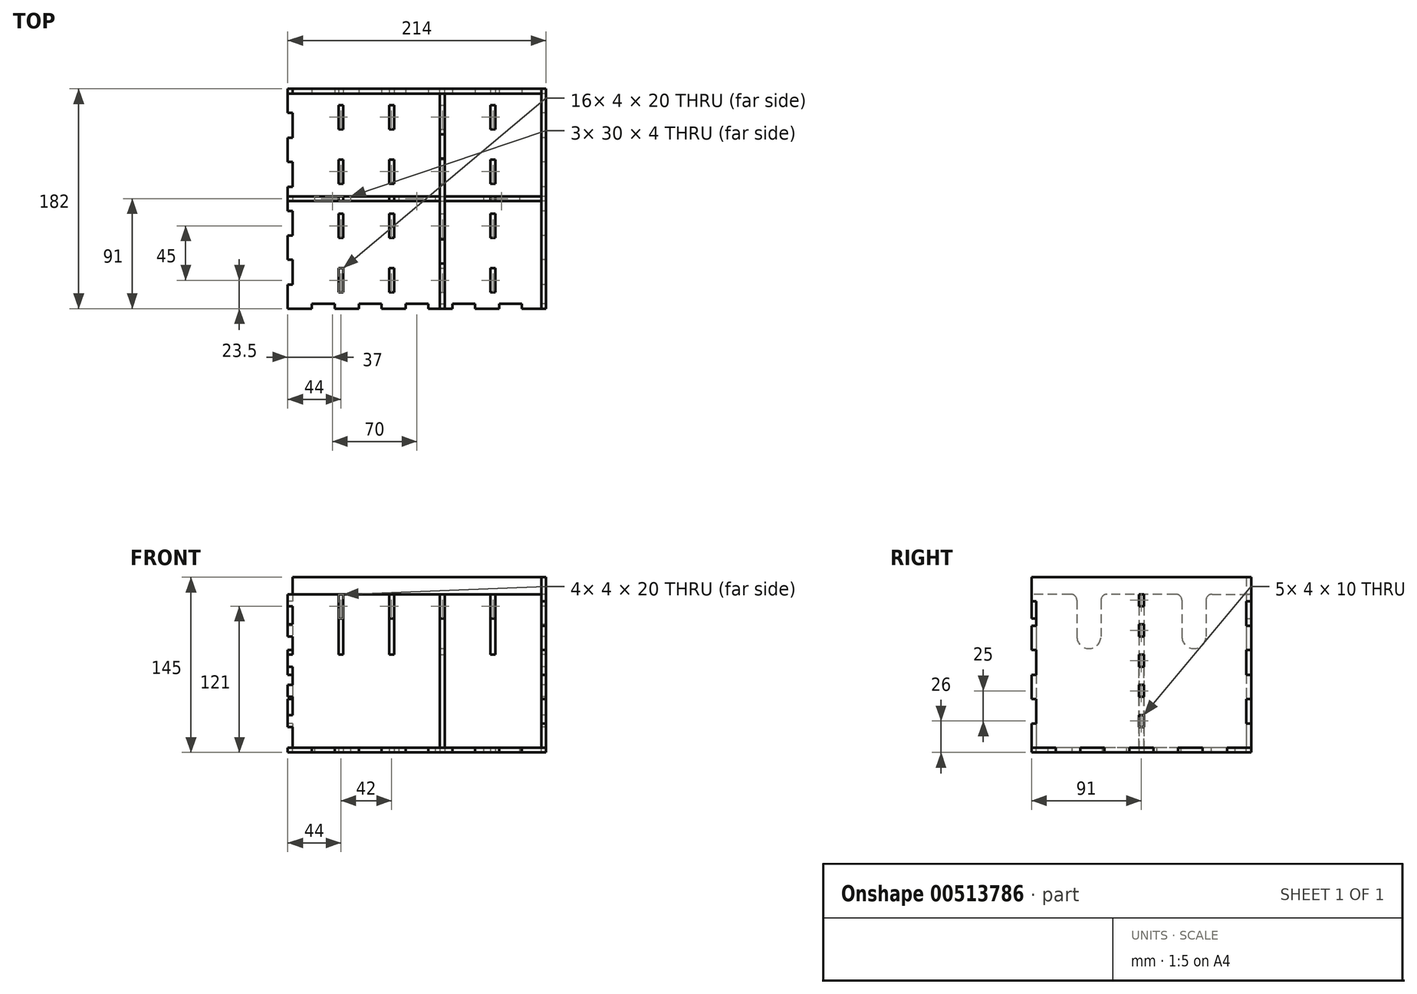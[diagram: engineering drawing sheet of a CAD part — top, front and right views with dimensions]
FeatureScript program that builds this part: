
annotation { "Feature Type Name" : "Feature", "Feature Type Description" : "" }
export const myFeature = defineFeature(function(context is Context, id is Id, definition is map)
    precondition{}
    {
        {
            assignVariable(context, id + "F0", {"name" : "mat_width", "anyValue" : 4});
        }
        {
            var Q0;
            Q0=qCreatedBy(makeId("Top.planeOp"),FACE);
            var sketch = newSketch(context, id + "F1", { "sketchPlane" : qUnion([Q0])});
            skLineSegment(sketch, "E0.bottom", {"start": v(-103, 87) * mm, "end": v(103, 87) * mm});
            skLineSegment(sketch, "E0.top", {"start": v(-103, -87) * mm, "end": v(103, -87) * mm});
            skLineSegment(sketch, "E0.left", {"start": v(-103, 87) * mm, "end": v(-103, -87) * mm});
            skLineSegment(sketch, "E0.right", {"start": v(103, 87) * mm, "end": v(103, -87) * mm});
            skLineSegment(sketch, "E1", {"start": v(-183.64, 0) * mm, "end": v(168.46, 0) * mm, "construction": true});
            skLineSegment(sketch, "E2.bottom", {"start": v(-85, 2) * mm, "end": v(-55, 2) * mm});
            skLineSegment(sketch, "E2.top", {"start": v(-85, -2) * mm, "end": v(-55, -2) * mm});
            skLineSegment(sketch, "E2.left", {"start": v(-85, 2) * mm, "end": v(-85, -2) * mm});
            skLineSegment(sketch, "E2.right", {"start": v(-55, 2) * mm, "end": v(-55, -2) * mm});
            skLineSegment(sketch, "E3.bottom", {"start": v(-15, 2) * mm, "end": v(15, 2) * mm});
            skLineSegment(sketch, "E3.top", {"start": v(-15, -2) * mm, "end": v(15, -2) * mm});
            skLineSegment(sketch, "E3.left", {"start": v(-15, 2) * mm, "end": v(-15, -2) * mm});
            skLineSegment(sketch, "E3.right", {"start": v(15, 2) * mm, "end": v(15, -2) * mm});
            skLineSegment(sketch, "E4.bottom", {"start": v(55, 2) * mm, "end": v(85, 2) * mm});
            skLineSegment(sketch, "E4.top", {"start": v(55, -2) * mm, "end": v(85, -2) * mm});
            skLineSegment(sketch, "E4.left", {"start": v(55, 2) * mm, "end": v(55, -2) * mm});
            skLineSegment(sketch, "E4.right", {"start": v(85, 2) * mm, "end": v(85, -2) * mm});
            skLineSegment(sketch, "E5", {"start": v(-63, 118.4) * mm, "end": v(-63, -118.4) * mm, "construction": true});
            skLineSegment(sketch, "E6.bottom", {"start": v(-61, 77.5) * mm, "end": v(-65, 77.5) * mm});
            skLineSegment(sketch, "E6.top", {"start": v(-61, 57.5) * mm, "end": v(-65, 57.5) * mm});
            skLineSegment(sketch, "E6.left", {"start": v(-61, 77.5) * mm, "end": v(-61, 57.5) * mm});
            skLineSegment(sketch, "E6.right", {"start": v(-65, 77.5) * mm, "end": v(-65, 57.5) * mm});
            skLineSegment(sketch, "E7.bottom", {"start": v(-65, 32.5) * mm, "end": v(-61, 32.5) * mm});
            skLineSegment(sketch, "E7.top", {"start": v(-65, 12.5) * mm, "end": v(-61, 12.5) * mm});
            skLineSegment(sketch, "E7.left", {"start": v(-65, 32.5) * mm, "end": v(-65, 12.5) * mm});
            skLineSegment(sketch, "E7.right", {"start": v(-61, 32.5) * mm, "end": v(-61, 12.5) * mm});
            skLineSegment(sketch, "E8.bottom", {"start": v(-65, -12.5) * mm, "end": v(-61, -12.5) * mm});
            skLineSegment(sketch, "E8.top", {"start": v(-65, -32.5) * mm, "end": v(-61, -32.5) * mm});
            skLineSegment(sketch, "E8.left", {"start": v(-65, -12.5) * mm, "end": v(-65, -32.5) * mm});
            skLineSegment(sketch, "E8.right", {"start": v(-61, -12.5) * mm, "end": v(-61, -32.5) * mm});
            skLineSegment(sketch, "E9.bottom", {"start": v(-65, -57.5) * mm, "end": v(-61, -57.5) * mm});
            skLineSegment(sketch, "E9.top", {"start": v(-65, -77.5) * mm, "end": v(-61, -77.5) * mm});
            skLineSegment(sketch, "E9.left", {"start": v(-65, -57.5) * mm, "end": v(-65, -77.5) * mm});
            skLineSegment(sketch, "E9.right", {"start": v(-61, -57.5) * mm, "end": v(-61, -77.5) * mm});
            skLineSegment(sketch, "E10.1.0.0", {"start": v(-21, 118.4) * mm, "end": v(-21, -118.4) * mm, "construction": true});
            skLineSegment(sketch, "E10.1.0.1", {"start": v(-23, 32.5) * mm, "end": v(-23, 12.5) * mm});
            skLineSegment(sketch, "E10.1.0.2", {"start": v(-23, 77.5) * mm, "end": v(-23, 57.5) * mm});
            skLineSegment(sketch, "E10.1.0.3", {"start": v(-19, 77.5) * mm, "end": v(-19, 57.5) * mm});
            skLineSegment(sketch, "E10.1.0.4", {"start": v(-19, 32.5) * mm, "end": v(-19, 12.5) * mm});
            skLineSegment(sketch, "E10.1.0.5", {"start": v(-19, 57.5) * mm, "end": v(-23, 57.5) * mm});
            skLineSegment(sketch, "E10.1.0.6", {"start": v(-23, 12.5) * mm, "end": v(-19, 12.5) * mm});
            skLineSegment(sketch, "E10.1.0.7", {"start": v(-23, 32.5) * mm, "end": v(-19, 32.5) * mm});
            skLineSegment(sketch, "E10.1.0.8", {"start": v(-19, 77.5) * mm, "end": v(-23, 77.5) * mm});
            skLineSegment(sketch, "E10.1.0.9", {"start": v(-23, -12.5) * mm, "end": v(-23, -32.5) * mm});
            skLineSegment(sketch, "E10.1.0.10", {"start": v(-23, -57.5) * mm, "end": v(-23, -77.5) * mm});
            skLineSegment(sketch, "E10.1.0.11", {"start": v(-19, -12.5) * mm, "end": v(-19, -32.5) * mm});
            skLineSegment(sketch, "E10.1.0.12", {"start": v(-19, -57.5) * mm, "end": v(-19, -77.5) * mm});
            skLineSegment(sketch, "E10.1.0.13", {"start": v(-23, -57.5) * mm, "end": v(-19, -57.5) * mm});
            skLineSegment(sketch, "E10.1.0.14", {"start": v(-23, -32.5) * mm, "end": v(-19, -32.5) * mm});
            skLineSegment(sketch, "E10.1.0.15", {"start": v(-23, -12.5) * mm, "end": v(-19, -12.5) * mm});
            skLineSegment(sketch, "E10.1.0.16", {"start": v(-23, -77.5) * mm, "end": v(-19, -77.5) * mm});
            skLineSegment(sketch, "E10.2.0.0", {"start": v(21, 118.4) * mm, "end": v(21, -118.4) * mm, "construction": true});
            skLineSegment(sketch, "E10.2.0.1", {"start": v(19, 32.5) * mm, "end": v(19, 12.5) * mm});
            skLineSegment(sketch, "E10.2.0.2", {"start": v(19, 77.5) * mm, "end": v(19, 57.5) * mm});
            skLineSegment(sketch, "E10.2.0.3", {"start": v(23, 77.5) * mm, "end": v(23, 57.5) * mm});
            skLineSegment(sketch, "E10.2.0.4", {"start": v(23, 32.5) * mm, "end": v(23, 12.5) * mm});
            skLineSegment(sketch, "E10.2.0.5", {"start": v(23, 57.5) * mm, "end": v(19, 57.5) * mm});
            skLineSegment(sketch, "E10.2.0.6", {"start": v(19, 12.5) * mm, "end": v(23, 12.5) * mm});
            skLineSegment(sketch, "E10.2.0.7", {"start": v(19, 32.5) * mm, "end": v(23, 32.5) * mm});
            skLineSegment(sketch, "E10.2.0.8", {"start": v(23, 77.5) * mm, "end": v(19, 77.5) * mm});
            skLineSegment(sketch, "E10.2.0.9", {"start": v(19, -12.5) * mm, "end": v(19, -32.5) * mm});
            skLineSegment(sketch, "E10.2.0.10", {"start": v(19, -57.5) * mm, "end": v(19, -77.5) * mm});
            skLineSegment(sketch, "E10.2.0.11", {"start": v(23, -12.5) * mm, "end": v(23, -32.5) * mm});
            skLineSegment(sketch, "E10.2.0.12", {"start": v(23, -57.5) * mm, "end": v(23, -77.5) * mm});
            skLineSegment(sketch, "E10.2.0.13", {"start": v(19, -57.5) * mm, "end": v(23, -57.5) * mm});
            skLineSegment(sketch, "E10.2.0.14", {"start": v(19, -32.5) * mm, "end": v(23, -32.5) * mm});
            skLineSegment(sketch, "E10.2.0.15", {"start": v(19, -12.5) * mm, "end": v(23, -12.5) * mm});
            skLineSegment(sketch, "E10.2.0.16", {"start": v(19, -77.5) * mm, "end": v(23, -77.5) * mm});
            skLineSegment(sketch, "E10.3.0.0", {"start": v(63, 118.4) * mm, "end": v(63, -118.4) * mm, "construction": true});
            skLineSegment(sketch, "E10.3.0.1", {"start": v(61, 32.5) * mm, "end": v(61, 12.5) * mm});
            skLineSegment(sketch, "E10.3.0.2", {"start": v(61, 77.5) * mm, "end": v(61, 57.5) * mm});
            skLineSegment(sketch, "E10.3.0.3", {"start": v(65, 77.5) * mm, "end": v(65, 57.5) * mm});
            skLineSegment(sketch, "E10.3.0.4", {"start": v(65, 32.5) * mm, "end": v(65, 12.5) * mm});
            skLineSegment(sketch, "E10.3.0.5", {"start": v(65, 57.5) * mm, "end": v(61, 57.5) * mm});
            skLineSegment(sketch, "E10.3.0.6", {"start": v(61, 12.5) * mm, "end": v(65, 12.5) * mm});
            skLineSegment(sketch, "E10.3.0.7", {"start": v(61, 32.5) * mm, "end": v(65, 32.5) * mm});
            skLineSegment(sketch, "E10.3.0.8", {"start": v(65, 77.5) * mm, "end": v(61, 77.5) * mm});
            skLineSegment(sketch, "E10.3.0.9", {"start": v(61, -12.5) * mm, "end": v(61, -32.5) * mm});
            skLineSegment(sketch, "E10.3.0.10", {"start": v(61, -57.5) * mm, "end": v(61, -77.5) * mm});
            skLineSegment(sketch, "E10.3.0.11", {"start": v(65, -12.5) * mm, "end": v(65, -32.5) * mm});
            skLineSegment(sketch, "E10.3.0.12", {"start": v(65, -57.5) * mm, "end": v(65, -77.5) * mm});
            skLineSegment(sketch, "E10.3.0.13", {"start": v(61, -57.5) * mm, "end": v(65, -57.5) * mm});
            skLineSegment(sketch, "E10.3.0.14", {"start": v(61, -32.5) * mm, "end": v(65, -32.5) * mm});
            skLineSegment(sketch, "E10.3.0.15", {"start": v(61, -12.5) * mm, "end": v(65, -12.5) * mm});
            skLineSegment(sketch, "E10.3.0.16", {"start": v(61, -77.5) * mm, "end": v(65, -77.5) * mm});
            skLineSegment(sketch, "E10.direction1", {"start": v(-63, -118.4) * mm, "end": v(-21, -118.4) * mm, "construction": true});
            skSolve(sketch);
        }
        {
            var Q0;
            Q0 = qSketchRegion(id + "F1", true);
            extrude(context, id + "F2", {"entities" : qUnion([Q0]), "depth" : (getVariable(context, 'mat_width')) * mm});
        }
        {
            var Q0;
            Q0=makeQuery(id+"F2.opExtrude","CAP_FACE",FACE,{"disambiguationData":[OSD([sQuery(id+"F1.wireOp",EDGE,"E0.bottom"),sQuery(id+"F1.wireOp",EDGE,"E0.top"),sQuery(id+"F1.wireOp",EDGE,"E0.left"),sQuery(id+"F1.wireOp",EDGE,"E0.right"),sQuery(id+"F1.wireOp",EDGE,"E2.bottom"),sQuery(id+"F1.wireOp",EDGE,"E2.top"),sQuery(id+"F1.wireOp",EDGE,"E2.left"),sQuery(id+"F1.wireOp",EDGE,"E2.right"),sQuery(id+"F1.wireOp",EDGE,"E3.bottom"),sQuery(id+"F1.wireOp",EDGE,"E3.top"),sQuery(id+"F1.wireOp",EDGE,"E3.left"),sQuery(id+"F1.wireOp",EDGE,"E3.right"),sQuery(id+"F1.wireOp",EDGE,"E4.bottom"),sQuery(id+"F1.wireOp",EDGE,"E4.top"),sQuery(id+"F1.wireOp",EDGE,"E4.left"),sQuery(id+"F1.wireOp",EDGE,"E4.right"),sQuery(id+"F1.wireOp",EDGE,"E6.bottom"),sQuery(id+"F1.wireOp",EDGE,"E6.top"),sQuery(id+"F1.wireOp",EDGE,"E6.left"),sQuery(id+"F1.wireOp",EDGE,"E6.right"),sQuery(id+"F1.wireOp",EDGE,"E7.bottom"),sQuery(id+"F1.wireOp",EDGE,"E7.top"),sQuery(id+"F1.wireOp",EDGE,"E7.left"),sQuery(id+"F1.wireOp",EDGE,"E7.right"),sQuery(id+"F1.wireOp",EDGE,"E8.bottom"),sQuery(id+"F1.wireOp",EDGE,"E8.top"),sQuery(id+"F1.wireOp",EDGE,"E8.left"),sQuery(id+"F1.wireOp",EDGE,"E8.right"),sQuery(id+"F1.wireOp",EDGE,"E9.bottom"),sQuery(id+"F1.wireOp",EDGE,"E9.top"),sQuery(id+"F1.wireOp",EDGE,"E9.left"),sQuery(id+"F1.wireOp",EDGE,"E9.right"),sQuery(id+"F1.wireOp",EDGE,"E10.1.0.1"),sQuery(id+"F1.wireOp",EDGE,"E10.1.0.2"),sQuery(id+"F1.wireOp",EDGE,"E10.1.0.3"),sQuery(id+"F1.wireOp",EDGE,"E10.1.0.4"),sQuery(id+"F1.wireOp",EDGE,"E10.1.0.5"),sQuery(id+"F1.wireOp",EDGE,"E10.1.0.6"),sQuery(id+"F1.wireOp",EDGE,"E10.1.0.7"),sQuery(id+"F1.wireOp",EDGE,"E10.1.0.8"),sQuery(id+"F1.wireOp",EDGE,"E10.1.0.9"),sQuery(id+"F1.wireOp",EDGE,"E10.1.0.10"),sQuery(id+"F1.wireOp",EDGE,"E10.1.0.11"),sQuery(id+"F1.wireOp",EDGE,"E10.1.0.12"),sQuery(id+"F1.wireOp",EDGE,"E10.1.0.13"),sQuery(id+"F1.wireOp",EDGE,"E10.1.0.14"),sQuery(id+"F1.wireOp",EDGE,"E10.1.0.15"),sQuery(id+"F1.wireOp",EDGE,"E10.1.0.16"),sQuery(id+"F1.wireOp",EDGE,"E10.2.0.1"),sQuery(id+"F1.wireOp",EDGE,"E10.2.0.2"),sQuery(id+"F1.wireOp",EDGE,"E10.2.0.3"),sQuery(id+"F1.wireOp",EDGE,"E10.2.0.4"),sQuery(id+"F1.wireOp",EDGE,"E10.2.0.5"),sQuery(id+"F1.wireOp",EDGE,"E10.2.0.6"),sQuery(id+"F1.wireOp",EDGE,"E10.2.0.7"),sQuery(id+"F1.wireOp",EDGE,"E10.2.0.8"),sQuery(id+"F1.wireOp",EDGE,"E10.2.0.9"),sQuery(id+"F1.wireOp",EDGE,"E10.2.0.10"),sQuery(id+"F1.wireOp",EDGE,"E10.2.0.11"),sQuery(id+"F1.wireOp",EDGE,"E10.2.0.12"),sQuery(id+"F1.wireOp",EDGE,"E10.2.0.13"),sQuery(id+"F1.wireOp",EDGE,"E10.2.0.14"),sQuery(id+"F1.wireOp",EDGE,"E10.2.0.15"),sQuery(id+"F1.wireOp",EDGE,"E10.2.0.16"),sQuery(id+"F1.wireOp",EDGE,"E10.3.0.1"),sQuery(id+"F1.wireOp",EDGE,"E10.3.0.2"),sQuery(id+"F1.wireOp",EDGE,"E10.3.0.3"),sQuery(id+"F1.wireOp",EDGE,"E10.3.0.4"),sQuery(id+"F1.wireOp",EDGE,"E10.3.0.5"),sQuery(id+"F1.wireOp",EDGE,"E10.3.0.6"),sQuery(id+"F1.wireOp",EDGE,"E10.3.0.7"),sQuery(id+"F1.wireOp",EDGE,"E10.3.0.8"),sQuery(id+"F1.wireOp",EDGE,"E10.3.0.9"),sQuery(id+"F1.wireOp",EDGE,"E10.3.0.10"),sQuery(id+"F1.wireOp",EDGE,"E10.3.0.11"),sQuery(id+"F1.wireOp",EDGE,"E10.3.0.12"),sQuery(id+"F1.wireOp",EDGE,"E10.3.0.13"),sQuery(id+"F1.wireOp",EDGE,"E10.3.0.14"),sQuery(id+"F1.wireOp",EDGE,"E10.3.0.15"),sQuery(id+"F1.wireOp",EDGE,"E10.3.0.16")])],"isStart":false});
            var sketch = newSketch(context, id + "F3", { "sketchPlane" : qUnion([Q0])});
            skLineSegment(sketch, "E11.bottom", {"start": v(-107, 91) * mm, "end": v(-103, 91) * mm});
            skLineSegment(sketch, "E11.top", {"start": v(-107, 71) * mm, "end": v(-103, 71) * mm});
            skLineSegment(sketch, "E11.left", {"start": v(-107, 91) * mm, "end": v(-107, 71) * mm});
            skLineSegment(sketch, "E11.right", {"start": v(-103, 91) * mm, "end": v(-103, 71) * mm});
            skLineSegment(sketch, "E12.bottom", {"start": v(-107, 91) * mm, "end": v(-87, 91) * mm});
            skLineSegment(sketch, "E12.top", {"start": v(-107, 87) * mm, "end": v(-87, 87) * mm});
            skLineSegment(sketch, "E12.left", {"start": v(-107, 91) * mm, "end": v(-107, 87) * mm});
            skLineSegment(sketch, "E12.right", {"start": v(-87, 91) * mm, "end": v(-87, 87) * mm});
            skLineSegment(sketch, "E13.1.0.0", {"start": v(-68.2, 91) * mm, "end": v(-68.2, 87) * mm});
            skLineSegment(sketch, "E13.1.0.1", {"start": v(-68.2, 87) * mm, "end": v(-48.2, 87) * mm});
            skLineSegment(sketch, "E13.1.0.2", {"start": v(-48.2, 91) * mm, "end": v(-48.2, 87) * mm});
            skLineSegment(sketch, "E13.1.0.3", {"start": v(-68.2, 91) * mm, "end": v(-48.2, 91) * mm});
            skLineSegment(sketch, "E13.2.0.0", {"start": v(-29.4, 91) * mm, "end": v(-29.4, 87) * mm});
            skLineSegment(sketch, "E13.2.0.1", {"start": v(-29.4, 87) * mm, "end": v(-9.4, 87) * mm});
            skLineSegment(sketch, "E13.2.0.2", {"start": v(-9.4, 91) * mm, "end": v(-9.4, 87) * mm});
            skLineSegment(sketch, "E13.2.0.3", {"start": v(-29.4, 91) * mm, "end": v(-9.4, 91) * mm});
            skLineSegment(sketch, "E13.3.0.0", {"start": v(9.4, 91) * mm, "end": v(9.4, 87) * mm});
            skLineSegment(sketch, "E13.3.0.1", {"start": v(9.4, 87) * mm, "end": v(29.4, 87) * mm});
            skLineSegment(sketch, "E13.3.0.2", {"start": v(29.4, 91) * mm, "end": v(29.4, 87) * mm});
            skLineSegment(sketch, "E13.3.0.3", {"start": v(9.4, 91) * mm, "end": v(29.4, 91) * mm});
            skLineSegment(sketch, "E13.4.0.0", {"start": v(48.2, 91) * mm, "end": v(48.2, 87) * mm});
            skLineSegment(sketch, "E13.4.0.1", {"start": v(48.2, 87) * mm, "end": v(68.2, 87) * mm});
            skLineSegment(sketch, "E13.4.0.2", {"start": v(68.2, 91) * mm, "end": v(68.2, 87) * mm});
            skLineSegment(sketch, "E13.4.0.3", {"start": v(48.2, 91) * mm, "end": v(68.2, 91) * mm});
            skLineSegment(sketch, "E13.5.0.0", {"start": v(87, 91) * mm, "end": v(87, 87) * mm});
            skLineSegment(sketch, "E13.5.0.1", {"start": v(87, 87) * mm, "end": v(107, 87) * mm});
            skLineSegment(sketch, "E13.5.0.2", {"start": v(107, 91) * mm, "end": v(107, 87) * mm});
            skLineSegment(sketch, "E13.5.0.3", {"start": v(87, 91) * mm, "end": v(107, 91) * mm});
            skLineSegment(sketch, "E13.direction1", {"start": v(-107, 87) * mm, "end": v(-68.2, 87) * mm, "construction": true});
            skLineSegment(sketch, "E14.0.1.0", {"start": v(-107, 50.5) * mm, "end": v(-103, 50.5) * mm});
            skLineSegment(sketch, "E14.0.1.1", {"start": v(-107, 50.5) * mm, "end": v(-107, 30.5) * mm});
            skLineSegment(sketch, "E14.0.1.2", {"start": v(-103, 50.5) * mm, "end": v(-103, 30.5) * mm});
            skLineSegment(sketch, "E14.0.1.3", {"start": v(-107, 30.5) * mm, "end": v(-103, 30.5) * mm});
            skLineSegment(sketch, "E14.0.2.0", {"start": v(-107, 10) * mm, "end": v(-103, 10) * mm});
            skLineSegment(sketch, "E14.0.2.1", {"start": v(-107, 10) * mm, "end": v(-107, -10) * mm});
            skLineSegment(sketch, "E14.0.2.2", {"start": v(-103, 10) * mm, "end": v(-103, -10) * mm});
            skLineSegment(sketch, "E14.0.2.3", {"start": v(-107, -10) * mm, "end": v(-103, -10) * mm});
            skLineSegment(sketch, "E14.0.3.0", {"start": v(-107, -30.5) * mm, "end": v(-103, -30.5) * mm});
            skLineSegment(sketch, "E14.0.3.1", {"start": v(-107, -30.5) * mm, "end": v(-107, -50.5) * mm});
            skLineSegment(sketch, "E14.0.3.2", {"start": v(-103, -30.5) * mm, "end": v(-103, -50.5) * mm});
            skLineSegment(sketch, "E14.0.3.3", {"start": v(-107, -50.5) * mm, "end": v(-103, -50.5) * mm});
            skLineSegment(sketch, "E14.0.4.0", {"start": v(-107, -71) * mm, "end": v(-103, -71) * mm});
            skLineSegment(sketch, "E14.0.4.1", {"start": v(-107, -71) * mm, "end": v(-107, -91) * mm});
            skLineSegment(sketch, "E14.0.4.2", {"start": v(-103, -71) * mm, "end": v(-103, -91) * mm});
            skLineSegment(sketch, "E14.0.4.3", {"start": v(-107, -91) * mm, "end": v(-103, -91) * mm});
            skLineSegment(sketch, "E14.direction1", {"start": v(-107, 71) * mm, "end": v(-82, 71) * mm, "construction": true});
            skLineSegment(sketch, "E14.direction2", {"start": v(-107, 71) * mm, "end": v(-107, 30.5) * mm, "construction": true});
            skLineSegment(sketch, "E15.MirrorCS", {"start": v(107, 91) * mm, "end": v(103, 91) * mm});
            skLineSegment(sketch, "E16.MirrorCS", {"start": v(107, 71) * mm, "end": v(103, 71) * mm});
            skLineSegment(sketch, "E17.MirrorCS", {"start": v(107, 30.5) * mm, "end": v(103, 30.5) * mm});
            skLineSegment(sketch, "E18.MirrorCS", {"start": v(107, 50.5) * mm, "end": v(103, 50.5) * mm});
            skLineSegment(sketch, "E19.MirrorCS", {"start": v(107, -10) * mm, "end": v(103, -10) * mm});
            skLineSegment(sketch, "E20.MirrorCS", {"start": v(107, -91) * mm, "end": v(103, -91) * mm});
            skLineSegment(sketch, "E21.MirrorCS", {"start": v(107, -30.5) * mm, "end": v(103, -30.5) * mm});
            skLineSegment(sketch, "E22.MirrorCS", {"start": v(107, -71) * mm, "end": v(103, -71) * mm});
            skLineSegment(sketch, "E23.MirrorCS", {"start": v(107, 10) * mm, "end": v(103, 10) * mm});
            skLineSegment(sketch, "E24.MirrorCS", {"start": v(107, -50.5) * mm, "end": v(103, -50.5) * mm});
            skLineSegment(sketch, "E25.MirrorCS", {"start": v(107, 50.5) * mm, "end": v(107, 30.5) * mm});
            skLineSegment(sketch, "E26.MirrorCS", {"start": v(103, -71) * mm, "end": v(103, -91) * mm});
            skLineSegment(sketch, "E27.MirrorCS", {"start": v(107, -71) * mm, "end": v(107, -91) * mm});
            skLineSegment(sketch, "E28.MirrorCS", {"start": v(103, 10) * mm, "end": v(103, -10) * mm});
            skLineSegment(sketch, "E29.MirrorCS", {"start": v(107, -30.5) * mm, "end": v(107, -50.5) * mm});
            skLineSegment(sketch, "E30.MirrorCS", {"start": v(103, 50.5) * mm, "end": v(103, 30.5) * mm});
            skLineSegment(sketch, "E31.MirrorCS", {"start": v(107, 10) * mm, "end": v(107, -10) * mm});
            skLineSegment(sketch, "E32.MirrorCS", {"start": v(103, -30.5) * mm, "end": v(103, -50.5) * mm});
            skLineSegment(sketch, "E33.MirrorCS", {"start": v(107, 91) * mm, "end": v(107, 71) * mm});
            skLineSegment(sketch, "E34.MirrorCS", {"start": v(103, 91) * mm, "end": v(103, 71) * mm});
            skLineSegment(sketch, "E35.MirrorCS", {"start": v(107, -91) * mm, "end": v(107, -87) * mm});
            skLineSegment(sketch, "E36.MirrorCS", {"start": v(-107, -91) * mm, "end": v(-107, -87) * mm});
            skLineSegment(sketch, "E37.MirrorCS", {"start": v(-68.2, -91) * mm, "end": v(-68.2, -87) * mm});
            skLineSegment(sketch, "E38.MirrorCS", {"start": v(-48.2, -91) * mm, "end": v(-48.2, -87) * mm});
            skLineSegment(sketch, "E39.MirrorCS", {"start": v(-87, -91) * mm, "end": v(-87, -87) * mm});
            skLineSegment(sketch, "E40.MirrorCS", {"start": v(48.2, -91) * mm, "end": v(48.2, -87) * mm});
            skLineSegment(sketch, "E41.MirrorCS", {"start": v(-29.4, -91) * mm, "end": v(-29.4, -87) * mm});
            skLineSegment(sketch, "E42.MirrorCS", {"start": v(-9.4, -91) * mm, "end": v(-9.4, -87) * mm});
            skLineSegment(sketch, "E43.MirrorCS", {"start": v(29.4, -91) * mm, "end": v(29.4, -87) * mm});
            skLineSegment(sketch, "E44.MirrorCS", {"start": v(9.4, -91) * mm, "end": v(9.4, -87) * mm});
            skLineSegment(sketch, "E45.MirrorCS", {"start": v(68.2, -91) * mm, "end": v(68.2, -87) * mm});
            skLineSegment(sketch, "E46.MirrorCS", {"start": v(87, -91) * mm, "end": v(87, -87) * mm});
            skLineSegment(sketch, "E47.MirrorCS", {"start": v(-107, -87) * mm, "end": v(-87, -87) * mm});
            skLineSegment(sketch, "E48.MirrorCS", {"start": v(-68.2, -91) * mm, "end": v(-48.2, -91) * mm});
            skLineSegment(sketch, "E49.MirrorCS", {"start": v(-68.2, -87) * mm, "end": v(-48.2, -87) * mm});
            skLineSegment(sketch, "E50.MirrorCS", {"start": v(-107, -91) * mm, "end": v(-87, -91) * mm});
            skLineSegment(sketch, "E51.MirrorCS", {"start": v(-29.4, -91) * mm, "end": v(-9.4, -91) * mm});
            skLineSegment(sketch, "E52.MirrorCS", {"start": v(87, -91) * mm, "end": v(107, -91) * mm});
            skLineSegment(sketch, "E53.MirrorCS", {"start": v(87, -87) * mm, "end": v(107, -87) * mm});
            skLineSegment(sketch, "E54.MirrorCS", {"start": v(9.4, -91) * mm, "end": v(29.4, -91) * mm});
            skLineSegment(sketch, "E55.MirrorCS", {"start": v(-29.4, -87) * mm, "end": v(-9.4, -87) * mm});
            skLineSegment(sketch, "E56.MirrorCS", {"start": v(9.4, -87) * mm, "end": v(29.4, -87) * mm});
            skLineSegment(sketch, "E57.MirrorCS", {"start": v(48.2, -87) * mm, "end": v(68.2, -87) * mm});
            skLineSegment(sketch, "E58.MirrorCS", {"start": v(48.2, -91) * mm, "end": v(68.2, -91) * mm});
            skSolve(sketch);
        }
        {
            var Q0;
            Q0 = qSketchRegion(id + "F3", true);
            extrude(context, id + "F4", {"entities" : qUnion([Q0]), "operationType" : NewBodyOperationType.ADD, "oppositeDirection" : true, "depth" : (getVariable(context, 'mat_width')) * mm});
        }
        {
            var Q0;
            Q0=makeQuery(id+"F2.opExtrude","SWEPT_FACE",FACE,{"disambiguationData":[OSD([sQuery(id+"F1.wireOp",EDGE,"E3.top")])]});
            var sketch = newSketch(context, id + "F5", { "sketchPlane" : qUnion([Q0])});
            skLineSegment(sketch, "E59.bottom", {"start": v(-103, 131) * mm, "end": v(-65, 131) * mm});
            skLineSegment(sketch, "E59.top", {"start": v(-103, 4) * mm, "end": v(103, 4) * mm});
            skLineSegment(sketch, "E59.left", {"start": v(-103, 131) * mm, "end": v(-103, 4) * mm});
            skLineSegment(sketch, "E59.right", {"start": v(103, 131) * mm, "end": v(103, 4) * mm});
            skLineSegment(sketch, "E60.bottom", {"start": v(-103, 131) * mm, "end": v(-107, 131) * mm});
            skLineSegment(sketch, "E60.top", {"start": v(-103, 121) * mm, "end": v(-107, 121) * mm});
            skLineSegment(sketch, "E60.left", {"start": v(-103, 131) * mm, "end": v(-103, 121) * mm});
            skLineSegment(sketch, "E60.right", {"start": v(-107, 131) * mm, "end": v(-107, 121) * mm});
            skLineSegment(sketch, "E61.0.1.0", {"start": v(-103, 106) * mm, "end": v(-103, 96) * mm});
            skLineSegment(sketch, "E61.0.1.1", {"start": v(-103, 96) * mm, "end": v(-107, 96) * mm});
            skLineSegment(sketch, "E61.0.1.2", {"start": v(-107, 106) * mm, "end": v(-107, 96) * mm});
            skLineSegment(sketch, "E61.0.1.3", {"start": v(-103, 106) * mm, "end": v(-107, 106) * mm});
            skLineSegment(sketch, "E61.0.2.0", {"start": v(-103, 81) * mm, "end": v(-103, 71) * mm});
            skLineSegment(sketch, "E61.0.2.1", {"start": v(-103, 71) * mm, "end": v(-107, 71) * mm});
            skLineSegment(sketch, "E61.0.2.2", {"start": v(-107, 81) * mm, "end": v(-107, 71) * mm});
            skLineSegment(sketch, "E61.0.2.3", {"start": v(-103, 81) * mm, "end": v(-107, 81) * mm});
            skLineSegment(sketch, "E61.0.3.0", {"start": v(-103, 56) * mm, "end": v(-103, 46) * mm});
            skLineSegment(sketch, "E61.0.3.1", {"start": v(-103, 46) * mm, "end": v(-107, 46) * mm});
            skLineSegment(sketch, "E61.0.3.2", {"start": v(-107, 56) * mm, "end": v(-107, 46) * mm});
            skLineSegment(sketch, "E61.0.3.3", {"start": v(-103, 56) * mm, "end": v(-107, 56) * mm});
            skLineSegment(sketch, "E61.0.4.0", {"start": v(-103, 31) * mm, "end": v(-103, 21) * mm});
            skLineSegment(sketch, "E61.0.4.1", {"start": v(-103, 21) * mm, "end": v(-107, 21) * mm});
            skLineSegment(sketch, "E61.0.4.2", {"start": v(-107, 31) * mm, "end": v(-107, 21) * mm});
            skLineSegment(sketch, "E61.0.4.3", {"start": v(-103, 31) * mm, "end": v(-107, 31) * mm});
            skLineSegment(sketch, "E61.direction1", {"start": v(-107, 121) * mm, "end": v(-82, 121) * mm, "construction": true});
            skLineSegment(sketch, "E61.direction2", {"start": v(-107, 121) * mm, "end": v(-107, 96) * mm, "construction": true});
            skLineSegment(sketch, "E62.MirrorCS", {"start": v(103, 131) * mm, "end": v(107, 131) * mm});
            skLineSegment(sketch, "E63.MirrorCS", {"start": v(103, 21) * mm, "end": v(107, 21) * mm});
            skLineSegment(sketch, "E64.MirrorCS", {"start": v(103, 96) * mm, "end": v(107, 96) * mm});
            skLineSegment(sketch, "E65.MirrorCS", {"start": v(103, 71) * mm, "end": v(107, 71) * mm});
            skLineSegment(sketch, "E66.MirrorCS", {"start": v(103, 46) * mm, "end": v(107, 46) * mm});
            skLineSegment(sketch, "E67.MirrorCS", {"start": v(103, 31) * mm, "end": v(107, 31) * mm});
            skLineSegment(sketch, "E68.MirrorCS", {"start": v(103, 121) * mm, "end": v(107, 121) * mm});
            skLineSegment(sketch, "E69.MirrorCS", {"start": v(103, 106) * mm, "end": v(107, 106) * mm});
            skLineSegment(sketch, "E70.MirrorCS", {"start": v(103, 56) * mm, "end": v(107, 56) * mm});
            skLineSegment(sketch, "E71.MirrorCS", {"start": v(103, 81) * mm, "end": v(107, 81) * mm});
            skLineSegment(sketch, "E72.MirrorCS", {"start": v(107, 106) * mm, "end": v(107, 96) * mm});
            skLineSegment(sketch, "E73.MirrorCS", {"start": v(103, 31) * mm, "end": v(103, 21) * mm});
            skLineSegment(sketch, "E74.MirrorCS", {"start": v(103, 131) * mm, "end": v(103, 121) * mm});
            skLineSegment(sketch, "E75.MirrorCS", {"start": v(103, 81) * mm, "end": v(103, 71) * mm});
            skLineSegment(sketch, "E76.MirrorCS", {"start": v(103, 106) * mm, "end": v(103, 96) * mm});
            skLineSegment(sketch, "E77.MirrorCS", {"start": v(107, 131) * mm, "end": v(107, 121) * mm});
            skLineSegment(sketch, "E78.MirrorCS", {"start": v(107, 56) * mm, "end": v(107, 46) * mm});
            skLineSegment(sketch, "E79.MirrorCS", {"start": v(103, 56) * mm, "end": v(103, 46) * mm});
            skLineSegment(sketch, "E80.MirrorCS", {"start": v(107, 81) * mm, "end": v(107, 71) * mm});
            skLineSegment(sketch, "E81.MirrorCS", {"start": v(107, 31) * mm, "end": v(107, 21) * mm});
            skLineSegment(sketch, "E82.top", {"start": v(-65, 81) * mm, "end": v(-61, 81) * mm});
            skLineSegment(sketch, "E82.left", {"start": v(-65, 131) * mm, "end": v(-65, 81) * mm});
            skLineSegment(sketch, "E82.right", {"start": v(-61, 131) * mm, "end": v(-61, 81) * mm});
            skLineSegment(sketch, "E83.top", {"start": v(-23, 81) * mm, "end": v(-19, 81) * mm});
            skLineSegment(sketch, "E83.left", {"start": v(-23, 131) * mm, "end": v(-23, 81) * mm});
            skLineSegment(sketch, "E83.right", {"start": v(-19, 131) * mm, "end": v(-19, 81) * mm});
            skLineSegment(sketch, "E84.top", {"start": v(19, 81) * mm, "end": v(23, 81) * mm});
            skLineSegment(sketch, "E84.left", {"start": v(19, 131) * mm, "end": v(19, 81) * mm});
            skLineSegment(sketch, "E84.right", {"start": v(23, 131) * mm, "end": v(23, 81) * mm});
            skLineSegment(sketch, "E85.top", {"start": v(61, 81) * mm, "end": v(65, 81) * mm});
            skLineSegment(sketch, "E85.left", {"start": v(61, 131) * mm, "end": v(61, 81) * mm});
            skLineSegment(sketch, "E85.right", {"start": v(65, 131) * mm, "end": v(65, 81) * mm});
            skLineSegment(sketch, "E86.trimOffspring", {"start": v(-61, 131) * mm, "end": v(-23, 131) * mm});
            skLineSegment(sketch, "E87.trimOffspring", {"start": v(-19, 131) * mm, "end": v(19, 131) * mm});
            skLineSegment(sketch, "E88.trimOffspring", {"start": v(23, 131) * mm, "end": v(61, 131) * mm});
            skLineSegment(sketch, "E89.trimOffspring", {"start": v(65, 131) * mm, "end": v(103, 131) * mm});
            skLineSegment(sketch, "E90.bottom", {"start": v(-85, 4) * mm, "end": v(-55, 4) * mm});
            skLineSegment(sketch, "E90.top", {"start": v(-85, 0) * mm, "end": v(-55, 0) * mm});
            skLineSegment(sketch, "E90.left", {"start": v(-85, 4) * mm, "end": v(-85, 0) * mm});
            skLineSegment(sketch, "E90.right", {"start": v(-55, 4) * mm, "end": v(-55, 0) * mm});
            skLineSegment(sketch, "E91.bottom", {"start": v(-15, 4) * mm, "end": v(15, 4) * mm});
            skLineSegment(sketch, "E91.top", {"start": v(-15, 0) * mm, "end": v(15, 0) * mm});
            skLineSegment(sketch, "E91.left", {"start": v(-15, 4) * mm, "end": v(-15, 0) * mm});
            skLineSegment(sketch, "E91.right", {"start": v(15, 4) * mm, "end": v(15, 0) * mm});
            skLineSegment(sketch, "E92.bottom", {"start": v(55, 4) * mm, "end": v(85, 4) * mm});
            skLineSegment(sketch, "E92.top", {"start": v(55, 0) * mm, "end": v(85, 0) * mm});
            skLineSegment(sketch, "E92.left", {"start": v(55, 4) * mm, "end": v(55, 0) * mm});
            skLineSegment(sketch, "E92.right", {"start": v(85, 4) * mm, "end": v(85, 0) * mm});
            skSolve(sketch);
        }
        {
            var Q0;
            Q0 = qSketchRegion(id + "F5", true);
            extrude(context, id + "F6", {"entities" : qUnion([Q0]), "depth" : (getVariable(context, 'mat_width')) * mm});
        }
        {
            var Q0;
            Q0=makeQuery(id+"F2.opExtrude","SWEPT_FACE",FACE,{"disambiguationData":[OSD([sQuery(id+"F1.wireOp",EDGE,"E10.2.0.11")])]});
            var sketch = newSketch(context, id + "F7", { "sketchPlane" : qUnion([Q0])});
            skLineSegment(sketch, "E93.bottom", {"start": v(-87, 131) * mm, "end": v(-58.5, 131) * mm});
            skLineSegment(sketch, "E93.top", {"start": v(-87, 4) * mm, "end": v(-2, 4) * mm});
            skLineSegment(sketch, "E93.left", {"start": v(-87, 131) * mm, "end": v(-87, 4) * mm});
            skLineSegment(sketch, "E93.right", {"start": v(87, 131) * mm, "end": v(87, 4) * mm});
            skLineSegment(sketch, "E94.top", {"start": v(-2, 81) * mm, "end": v(2, 81) * mm});
            skLineSegment(sketch, "E94.left", {"start": v(-2, 4) * mm, "end": v(-2, 81) * mm});
            skLineSegment(sketch, "E94.right", {"start": v(2, 4) * mm, "end": v(2, 81) * mm});
            skLineSegment(sketch, "E95.trimOffspring", {"start": v(2, 4) * mm, "end": v(87, 4) * mm});
            skLineSegment(sketch, "E96.bottom", {"start": v(-87, 131) * mm, "end": v(-91, 131) * mm});
            skLineSegment(sketch, "E96.top", {"start": v(-87, 111) * mm, "end": v(-91, 111) * mm});
            skLineSegment(sketch, "E96.left", {"start": v(-87, 131) * mm, "end": v(-87, 111) * mm});
            skLineSegment(sketch, "E96.right", {"start": v(-91, 131) * mm, "end": v(-91, 111) * mm});
            skLineSegment(sketch, "E97.MirrorCS", {"start": v(87, 131) * mm, "end": v(87, 111) * mm});
            skLineSegment(sketch, "E98.MirrorCS", {"start": v(87, 111) * mm, "end": v(91, 111) * mm});
            skLineSegment(sketch, "E99.MirrorCS", {"start": v(91, 131) * mm, "end": v(91, 111) * mm});
            skLineSegment(sketch, "E100.MirrorCS", {"start": v(87, 131) * mm, "end": v(91, 131) * mm});
            skLineSegment(sketch, "E101.top", {"start": v(-53.5, 96) * mm, "end": v(-33.5, 96) * mm, "construction": true});
            skLineSegment(sketch, "E101.left", {"start": v(-53.5, 126) * mm, "end": v(-53.5, 96) * mm});
            skLineSegment(sketch, "E101.right", {"start": v(-33.5, 126) * mm, "end": v(-33.5, 96) * mm});
            skLineSegment(sketch, "E102", {"start": v(-43.5, 157.63) * mm, "end": v(-43.5, -79.9) * mm, "construction": true});
            skLineSegment(sketch, "E103", {"start": v(0, -78.02) * mm, "end": v(0, 157.9) * mm, "construction": true});
            skArc(sketch, "E104", {"start": v(-53.5, 96) * mm, "mid": v(-43.5, 86) * mm, "end": v(-33.5, 96) * mm});
            skArc(sketch, "E105.MirrorCS", {"start": v(53.5, 96) * mm, "mid": v(43.5, 86) * mm, "end": v(33.5, 96) * mm});
            skLineSegment(sketch, "E106.MirrorCS", {"start": v(33.5, 126) * mm, "end": v(33.5, 96) * mm});
            skLineSegment(sketch, "E107.MirrorCS", {"start": v(53.5, 126) * mm, "end": v(53.5, 96) * mm});
            skLineSegment(sketch, "E108.trimOffspring", {"start": v(-28.5, 131) * mm, "end": v(28.5, 131) * mm});
            skLineSegment(sketch, "E109.trimOffspring", {"start": v(58.5, 131) * mm, "end": v(87, 131) * mm});
            skLineSegment(sketch, "E110.bottom", {"start": v(-77.5, 4) * mm, "end": v(-57.5, 4) * mm});
            skLineSegment(sketch, "E110.top", {"start": v(-77.5, 0) * mm, "end": v(-57.5, 0) * mm});
            skLineSegment(sketch, "E110.left", {"start": v(-77.5, 4) * mm, "end": v(-77.5, 0) * mm});
            skLineSegment(sketch, "E110.right", {"start": v(-57.5, 4) * mm, "end": v(-57.5, 0) * mm});
            skLineSegment(sketch, "E111.bottom", {"start": v(-32.5, 4) * mm, "end": v(-12.5, 4) * mm});
            skLineSegment(sketch, "E111.top", {"start": v(-32.5, 0) * mm, "end": v(-12.5, 0) * mm});
            skLineSegment(sketch, "E111.left", {"start": v(-32.5, 4) * mm, "end": v(-32.5, 0) * mm});
            skLineSegment(sketch, "E111.right", {"start": v(-12.5, 4) * mm, "end": v(-12.5, 0) * mm});
            skLineSegment(sketch, "E112.bottom", {"start": v(12.5, 4) * mm, "end": v(32.5, 4) * mm});
            skLineSegment(sketch, "E112.top", {"start": v(12.5, 0) * mm, "end": v(32.5, 0) * mm});
            skLineSegment(sketch, "E112.left", {"start": v(12.5, 4) * mm, "end": v(12.5, 0) * mm});
            skLineSegment(sketch, "E112.right", {"start": v(32.5, 4) * mm, "end": v(32.5, 0) * mm});
            skLineSegment(sketch, "E113.bottom", {"start": v(57.5, 4) * mm, "end": v(77.5, 4) * mm});
            skLineSegment(sketch, "E113.top", {"start": v(57.5, 0) * mm, "end": v(77.5, 0) * mm});
            skLineSegment(sketch, "E113.left", {"start": v(57.5, 4) * mm, "end": v(57.5, 0) * mm});
            skLineSegment(sketch, "E113.right", {"start": v(77.5, 4) * mm, "end": v(77.5, 0) * mm});
            skPoint(sketch, "E114.visualSharp", {"position": v(-53.5, 131) * mm});
            skArc(sketch, "E114.filletArc", {"start": v(-53.5, 126) * mm, "mid": v(-54.96, 129.54) * mm, "end": v(-58.5, 131) * mm});
            skPoint(sketch, "E115.visualSharp", {"position": v(-33.5, 131) * mm});
            skArc(sketch, "E115.filletArc", {"start": v(-28.5, 131) * mm, "mid": v(-32.04, 129.54) * mm, "end": v(-33.5, 126) * mm});
            skPoint(sketch, "E116.visualSharp", {"position": v(33.5, 131) * mm});
            skArc(sketch, "E116.filletArc", {"start": v(33.5, 126) * mm, "mid": v(32.04, 129.54) * mm, "end": v(28.5, 131) * mm});
            skPoint(sketch, "E117.visualSharp", {"position": v(53.5, 131) * mm});
            skArc(sketch, "E117.filletArc", {"start": v(58.5, 131) * mm, "mid": v(54.96, 129.54) * mm, "end": v(53.5, 126) * mm});
            skSolve(sketch);
        }
        {
            var Q0;
            Q0 = qSketchRegion(id + "F7", true);
            extrude(context, id + "F8", {"entities" : qUnion([Q0]), "depth" : (getVariable(context, 'mat_width')) * mm});
        }
        {
            var Q0;
            {var subQ114=sQuery(id+"F1.wireOp",EDGE,"E0.right");var subQ148=sQuery(id+"F3.wireOp",EDGE,"E17.MirrorCS");Q0=makeQuery(id+"F4.boolean.opBoolean","SPLIT",FACE,{"disambiguationData":[TD([makeQuery(id+"F4.opExtrude","SWEPT_FACE",FACE,{"disambiguationData":[OSD([subQ148])]})])],"derivedFrom":makeQuery(id+"F2.opExtrude","SWEPT_FACE",FACE,{"disambiguationData":[OSD([subQ114])]})});}
            var sketch = newSketch(context, id + "F9", { "sketchPlane" : qUnion([Q0])});
            skLineSegment(sketch, "E118.bottom", {"start": v(-87, 145) * mm, "end": v(87, 145) * mm});
            skLineSegment(sketch, "E118.top", {"start": v(-87, 4) * mm, "end": v(87, 4) * mm});
            skLineSegment(sketch, "E118.left", {"start": v(-87, 145) * mm, "end": v(-87, 4) * mm});
            skLineSegment(sketch, "E118.right", {"start": v(87, 145) * mm, "end": v(87, 4) * mm});
            skLineSegment(sketch, "E119.bottom", {"start": v(-91, 145) * mm, "end": v(-87, 145) * mm});
            skLineSegment(sketch, "E119.top", {"start": v(-91, 125) * mm, "end": v(-87, 125) * mm});
            skLineSegment(sketch, "E119.left", {"start": v(-91, 145) * mm, "end": v(-91, 125) * mm});
            skLineSegment(sketch, "E119.right", {"start": v(-87, 145) * mm, "end": v(-87, 125) * mm});
            skLineSegment(sketch, "E120.0.1.0", {"start": v(-87, 104.67) * mm, "end": v(-87, 84.67) * mm});
            skLineSegment(sketch, "E120.0.1.1", {"start": v(-91, 104.67) * mm, "end": v(-87, 104.67) * mm});
            skLineSegment(sketch, "E120.0.1.2", {"start": v(-91, 84.67) * mm, "end": v(-87, 84.67) * mm});
            skLineSegment(sketch, "E120.0.1.3", {"start": v(-91, 104.67) * mm, "end": v(-91, 84.67) * mm});
            skLineSegment(sketch, "E120.0.2.0", {"start": v(-87, 64.33) * mm, "end": v(-87, 44.33) * mm});
            skLineSegment(sketch, "E120.0.2.1", {"start": v(-91, 64.33) * mm, "end": v(-87, 64.33) * mm});
            skLineSegment(sketch, "E120.0.2.2", {"start": v(-91, 44.33) * mm, "end": v(-87, 44.33) * mm});
            skLineSegment(sketch, "E120.0.2.3", {"start": v(-91, 64.33) * mm, "end": v(-91, 44.33) * mm});
            skLineSegment(sketch, "E120.0.3.0", {"start": v(-87, 24) * mm, "end": v(-87, 4) * mm});
            skLineSegment(sketch, "E120.0.3.1", {"start": v(-91, 24) * mm, "end": v(-87, 24) * mm});
            skLineSegment(sketch, "E120.0.3.2", {"start": v(-91, 4) * mm, "end": v(-87, 4) * mm});
            skLineSegment(sketch, "E120.0.3.3", {"start": v(-91, 24) * mm, "end": v(-91, 4) * mm});
            skLineSegment(sketch, "E120.direction1", {"start": v(-91, 125) * mm, "end": v(-66, 125) * mm, "construction": true});
            skLineSegment(sketch, "E120.direction2", {"start": v(-91, 125) * mm, "end": v(-91, 84.67) * mm, "construction": true});
            skLineSegment(sketch, "E121.MirrorCS", {"start": v(91, 125) * mm, "end": v(87, 125) * mm});
            skLineSegment(sketch, "E122.MirrorCS", {"start": v(91, 84.67) * mm, "end": v(87, 84.67) * mm});
            skLineSegment(sketch, "E123.MirrorCS", {"start": v(91, 24) * mm, "end": v(87, 24) * mm});
            skLineSegment(sketch, "E124.MirrorCS", {"start": v(91, 104.67) * mm, "end": v(87, 104.67) * mm});
            skLineSegment(sketch, "E125.MirrorCS", {"start": v(91, 145) * mm, "end": v(87, 145) * mm});
            skLineSegment(sketch, "E126.MirrorCS", {"start": v(91, 4) * mm, "end": v(87, 4) * mm});
            skLineSegment(sketch, "E127.MirrorCS", {"start": v(91, 64.33) * mm, "end": v(87, 64.33) * mm});
            skLineSegment(sketch, "E128.MirrorCS", {"start": v(91, 44.33) * mm, "end": v(87, 44.33) * mm});
            skLineSegment(sketch, "E129.MirrorCS", {"start": v(91, 104.67) * mm, "end": v(91, 84.67) * mm});
            skLineSegment(sketch, "E130.MirrorCS", {"start": v(87, 24) * mm, "end": v(87, 4) * mm});
            skLineSegment(sketch, "E131.MirrorCS", {"start": v(91, 24) * mm, "end": v(91, 4) * mm});
            skLineSegment(sketch, "E132.MirrorCS", {"start": v(87, 64.33) * mm, "end": v(87, 44.33) * mm});
            skLineSegment(sketch, "E133.MirrorCS", {"start": v(87, 104.67) * mm, "end": v(87, 84.67) * mm});
            skLineSegment(sketch, "E134.MirrorCS", {"start": v(87, 145) * mm, "end": v(87, 125) * mm});
            skLineSegment(sketch, "E135.MirrorCS", {"start": v(91, 64.33) * mm, "end": v(91, 44.33) * mm});
            skLineSegment(sketch, "E136.MirrorCS", {"start": v(91, 145) * mm, "end": v(91, 125) * mm});
            skLineSegment(sketch, "E137", {"start": v(0, 148.8) * mm, "end": v(0, -32.08) * mm, "construction": true});
            skLineSegment(sketch, "E138.bottom", {"start": v(-71, 4) * mm, "end": v(-50.5, 4) * mm});
            skLineSegment(sketch, "E138.top", {"start": v(-71, 0) * mm, "end": v(-50.5, 0) * mm});
            skLineSegment(sketch, "E138.left", {"start": v(-71, 4) * mm, "end": v(-71, 0) * mm});
            skLineSegment(sketch, "E138.right", {"start": v(-50.5, 4) * mm, "end": v(-50.5, 0) * mm});
            skLineSegment(sketch, "E139.bottom", {"start": v(-30.5, 4) * mm, "end": v(-10, 4) * mm});
            skLineSegment(sketch, "E139.top", {"start": v(-30.5, 0) * mm, "end": v(-10, 0) * mm});
            skLineSegment(sketch, "E139.left", {"start": v(-30.5, 4) * mm, "end": v(-30.5, 0) * mm});
            skLineSegment(sketch, "E139.right", {"start": v(-10, 4) * mm, "end": v(-10, 0) * mm});
            skLineSegment(sketch, "E140.bottom", {"start": v(10, 4) * mm, "end": v(30.5, 4) * mm});
            skLineSegment(sketch, "E140.top", {"start": v(10, 0) * mm, "end": v(30.5, 0) * mm});
            skLineSegment(sketch, "E140.left", {"start": v(10, 4) * mm, "end": v(10, 0) * mm});
            skLineSegment(sketch, "E140.right", {"start": v(30.5, 4) * mm, "end": v(30.5, 0) * mm});
            skLineSegment(sketch, "E141.bottom", {"start": v(50.5, 4) * mm, "end": v(71, 4) * mm});
            skLineSegment(sketch, "E141.top", {"start": v(50.5, 0) * mm, "end": v(71, 0) * mm});
            skLineSegment(sketch, "E141.left", {"start": v(50.5, 4) * mm, "end": v(50.5, 0) * mm});
            skLineSegment(sketch, "E141.right", {"start": v(71, 4) * mm, "end": v(71, 0) * mm});
            skLineSegment(sketch, "E142.bottom", {"start": v(-2, 131) * mm, "end": v(2, 131) * mm});
            skLineSegment(sketch, "E142.top", {"start": v(-2, 121) * mm, "end": v(2, 121) * mm});
            skLineSegment(sketch, "E142.left", {"start": v(-2, 131) * mm, "end": v(-2, 121) * mm});
            skLineSegment(sketch, "E142.right", {"start": v(2, 131) * mm, "end": v(2, 121) * mm});
            skLineSegment(sketch, "E143.bottom", {"start": v(-2, 106) * mm, "end": v(2, 106) * mm});
            skLineSegment(sketch, "E143.top", {"start": v(-2, 96) * mm, "end": v(2, 96) * mm});
            skLineSegment(sketch, "E143.left", {"start": v(-2, 106) * mm, "end": v(-2, 96) * mm});
            skLineSegment(sketch, "E143.right", {"start": v(2, 106) * mm, "end": v(2, 96) * mm});
            skLineSegment(sketch, "E144.bottom", {"start": v(-2, 81) * mm, "end": v(2, 81) * mm});
            skLineSegment(sketch, "E144.top", {"start": v(-2, 71) * mm, "end": v(2, 71) * mm});
            skLineSegment(sketch, "E144.left", {"start": v(-2, 81) * mm, "end": v(-2, 71) * mm});
            skLineSegment(sketch, "E144.right", {"start": v(2, 81) * mm, "end": v(2, 71) * mm});
            skLineSegment(sketch, "E145.bottom", {"start": v(-2, 56) * mm, "end": v(2, 56) * mm});
            skLineSegment(sketch, "E145.top", {"start": v(-2, 46) * mm, "end": v(2, 46) * mm});
            skLineSegment(sketch, "E145.left", {"start": v(-2, 56) * mm, "end": v(-2, 46) * mm});
            skLineSegment(sketch, "E145.right", {"start": v(2, 56) * mm, "end": v(2, 46) * mm});
            skLineSegment(sketch, "E146.bottom", {"start": v(-2, 31) * mm, "end": v(2, 31) * mm});
            skLineSegment(sketch, "E146.top", {"start": v(-2, 21) * mm, "end": v(2, 21) * mm});
            skLineSegment(sketch, "E146.left", {"start": v(-2, 31) * mm, "end": v(-2, 21) * mm});
            skLineSegment(sketch, "E146.right", {"start": v(2, 31) * mm, "end": v(2, 21) * mm});
            skSolve(sketch);
        }
        {
            var Q0;
            Q0 = qSketchRegion(id + "F9", true);
            extrude(context, id + "F10", {"entities" : qUnion([Q0]), "depth" : (getVariable(context, 'mat_width')) * mm});
        }
        {
            var Q0;
            {var subQ33=sQuery(id+"F3.wireOp",EDGE,"E13.3.0.2");var subQ113=sQuery(id+"F1.wireOp",EDGE,"E0.bottom");Q0=makeQuery(id+"F4.boolean.opBoolean","SPLIT",FACE,{"disambiguationData":[TD([makeQuery(id+"F4.opExtrude","SWEPT_FACE",FACE,{"disambiguationData":[OSD([subQ33])]})])],"derivedFrom":makeQuery(id+"F2.opExtrude","SWEPT_FACE",FACE,{"disambiguationData":[OSD([subQ113])]})});}
            var sketch = newSketch(context, id + "F11", { "sketchPlane" : qUnion([Q0])});
            skLineSegment(sketch, "E147.bottom", {"start": v(-103, 145) * mm, "end": v(103, 145) * mm});
            skLineSegment(sketch, "E147.top", {"start": v(-103, 4) * mm, "end": v(103, 4) * mm});
            skLineSegment(sketch, "E147.left", {"start": v(-103, 145) * mm, "end": v(-103, 4) * mm});
            skLineSegment(sketch, "E147.right", {"start": v(103, 145) * mm, "end": v(103, 4) * mm});
            skLineSegment(sketch, "E148.bottom", {"start": v(-103, 125) * mm, "end": v(-107, 125) * mm});
            skLineSegment(sketch, "E148.top", {"start": v(-103, 104.67) * mm, "end": v(-107, 104.67) * mm});
            skLineSegment(sketch, "E148.left", {"start": v(-103, 125) * mm, "end": v(-103, 104.67) * mm});
            skLineSegment(sketch, "E148.right", {"start": v(-107, 125) * mm, "end": v(-107, 104.67) * mm});
            skLineSegment(sketch, "E149.bottom", {"start": v(-103, 84.67) * mm, "end": v(-107, 84.67) * mm});
            skLineSegment(sketch, "E149.top", {"start": v(-103, 64.33) * mm, "end": v(-107, 64.33) * mm});
            skLineSegment(sketch, "E149.left", {"start": v(-103, 84.67) * mm, "end": v(-103, 64.33) * mm});
            skLineSegment(sketch, "E149.right", {"start": v(-107, 84.67) * mm, "end": v(-107, 64.33) * mm});
            skLineSegment(sketch, "E150.bottom", {"start": v(-103, 44.33) * mm, "end": v(-107, 44.33) * mm});
            skLineSegment(sketch, "E150.top", {"start": v(-103, 24) * mm, "end": v(-107, 24) * mm});
            skLineSegment(sketch, "E150.left", {"start": v(-103, 44.33) * mm, "end": v(-103, 24) * mm});
            skLineSegment(sketch, "E150.right", {"start": v(-107, 44.33) * mm, "end": v(-107, 24) * mm});
            skLineSegment(sketch, "E151.MirrorCS", {"start": v(103, 44.33) * mm, "end": v(107, 44.33) * mm});
            skLineSegment(sketch, "E152.MirrorCS", {"start": v(103, 64.33) * mm, "end": v(107, 64.33) * mm});
            skLineSegment(sketch, "E153.MirrorCS", {"start": v(103, 24) * mm, "end": v(107, 24) * mm});
            skLineSegment(sketch, "E154.MirrorCS", {"start": v(103, 125) * mm, "end": v(107, 125) * mm});
            skLineSegment(sketch, "E155.MirrorCS", {"start": v(103, 104.67) * mm, "end": v(107, 104.67) * mm});
            skLineSegment(sketch, "E156.MirrorCS", {"start": v(103, 84.67) * mm, "end": v(107, 84.67) * mm});
            skLineSegment(sketch, "E157.MirrorCS", {"start": v(107, 44.33) * mm, "end": v(107, 24) * mm});
            skLineSegment(sketch, "E158.MirrorCS", {"start": v(107, 84.67) * mm, "end": v(107, 64.33) * mm});
            skLineSegment(sketch, "E159.MirrorCS", {"start": v(103, 84.67) * mm, "end": v(103, 64.33) * mm});
            skLineSegment(sketch, "E160.MirrorCS", {"start": v(103, 44.33) * mm, "end": v(103, 24) * mm});
            skLineSegment(sketch, "E161.MirrorCS", {"start": v(107, 125) * mm, "end": v(107, 104.67) * mm});
            skLineSegment(sketch, "E162.MirrorCS", {"start": v(103, 125) * mm, "end": v(103, 104.67) * mm});
            skLineSegment(sketch, "E163.bottom", {"start": v(-23, 131) * mm, "end": v(-19, 131) * mm});
            skLineSegment(sketch, "E163.top", {"start": v(-23, 111) * mm, "end": v(-19, 111) * mm});
            skLineSegment(sketch, "E163.left", {"start": v(-23, 131) * mm, "end": v(-23, 111) * mm});
            skLineSegment(sketch, "E163.right", {"start": v(-19, 131) * mm, "end": v(-19, 111) * mm});
            skLineSegment(sketch, "E164.bottom", {"start": v(-87, 4) * mm, "end": v(-68.2, 4) * mm});
            skLineSegment(sketch, "E164.top", {"start": v(-87, 0) * mm, "end": v(-68.2, 0) * mm});
            skLineSegment(sketch, "E164.left", {"start": v(-87, 4) * mm, "end": v(-87, 0) * mm});
            skLineSegment(sketch, "E164.right", {"start": v(-68.2, 4) * mm, "end": v(-68.2, 0) * mm});
            skLineSegment(sketch, "E165.bottom", {"start": v(-48.2, 4) * mm, "end": v(-29.4, 4) * mm});
            skLineSegment(sketch, "E165.top", {"start": v(-48.2, 0) * mm, "end": v(-29.4, 0) * mm});
            skLineSegment(sketch, "E165.left", {"start": v(-48.2, 4) * mm, "end": v(-48.2, 0) * mm});
            skLineSegment(sketch, "E165.right", {"start": v(-29.4, 4) * mm, "end": v(-29.4, 0) * mm});
            skLineSegment(sketch, "E166.bottom", {"start": v(-9.4, 4) * mm, "end": v(9.4, 4) * mm});
            skLineSegment(sketch, "E166.top", {"start": v(-9.4, 0) * mm, "end": v(9.4, 0) * mm});
            skLineSegment(sketch, "E166.left", {"start": v(-9.4, 4) * mm, "end": v(-9.4, 0) * mm});
            skLineSegment(sketch, "E166.right", {"start": v(9.4, 4) * mm, "end": v(9.4, 0) * mm});
            skLineSegment(sketch, "E167.bottom", {"start": v(29.4, 4) * mm, "end": v(48.2, 4) * mm});
            skLineSegment(sketch, "E167.top", {"start": v(29.4, 0) * mm, "end": v(48.2, 0) * mm});
            skLineSegment(sketch, "E167.left", {"start": v(29.4, 4) * mm, "end": v(29.4, 0) * mm});
            skLineSegment(sketch, "E167.right", {"start": v(48.2, 4) * mm, "end": v(48.2, 0) * mm});
            skLineSegment(sketch, "E168.bottom", {"start": v(68.2, 4) * mm, "end": v(87, 4) * mm});
            skLineSegment(sketch, "E168.top", {"start": v(68.2, 0) * mm, "end": v(87, 0) * mm});
            skLineSegment(sketch, "E168.left", {"start": v(68.2, 4) * mm, "end": v(68.2, 0) * mm});
            skLineSegment(sketch, "E168.right", {"start": v(87, 4) * mm, "end": v(87, 0) * mm});
            skLineSegment(sketch, "E169.bottom", {"start": v(-65, 131) * mm, "end": v(-61, 131) * mm});
            skLineSegment(sketch, "E169.top", {"start": v(-65, 111) * mm, "end": v(-61, 111) * mm});
            skLineSegment(sketch, "E169.left", {"start": v(-65, 131) * mm, "end": v(-65, 111) * mm});
            skLineSegment(sketch, "E169.right", {"start": v(-61, 131) * mm, "end": v(-61, 111) * mm});
            skLineSegment(sketch, "E170.bottom", {"start": v(19, 131) * mm, "end": v(23, 131) * mm});
            skLineSegment(sketch, "E170.top", {"start": v(19, 111) * mm, "end": v(23, 111) * mm});
            skLineSegment(sketch, "E170.left", {"start": v(19, 131) * mm, "end": v(19, 111) * mm});
            skLineSegment(sketch, "E170.right", {"start": v(23, 131) * mm, "end": v(23, 111) * mm});
            skLineSegment(sketch, "E171.bottom", {"start": v(61, 131) * mm, "end": v(65, 131) * mm});
            skLineSegment(sketch, "E171.top", {"start": v(61, 111) * mm, "end": v(65, 111) * mm});
            skLineSegment(sketch, "E171.left", {"start": v(61, 131) * mm, "end": v(61, 111) * mm});
            skLineSegment(sketch, "E171.right", {"start": v(65, 131) * mm, "end": v(65, 111) * mm});
            skSolve(sketch);
        }
        {
            var Q0;
            Q0 = qSketchRegion(id + "F11", true);
            extrude(context, id + "F12", {"entities" : qUnion([Q0]), "depth" : (getVariable(context, 'mat_width')) * mm});
        }
    });
